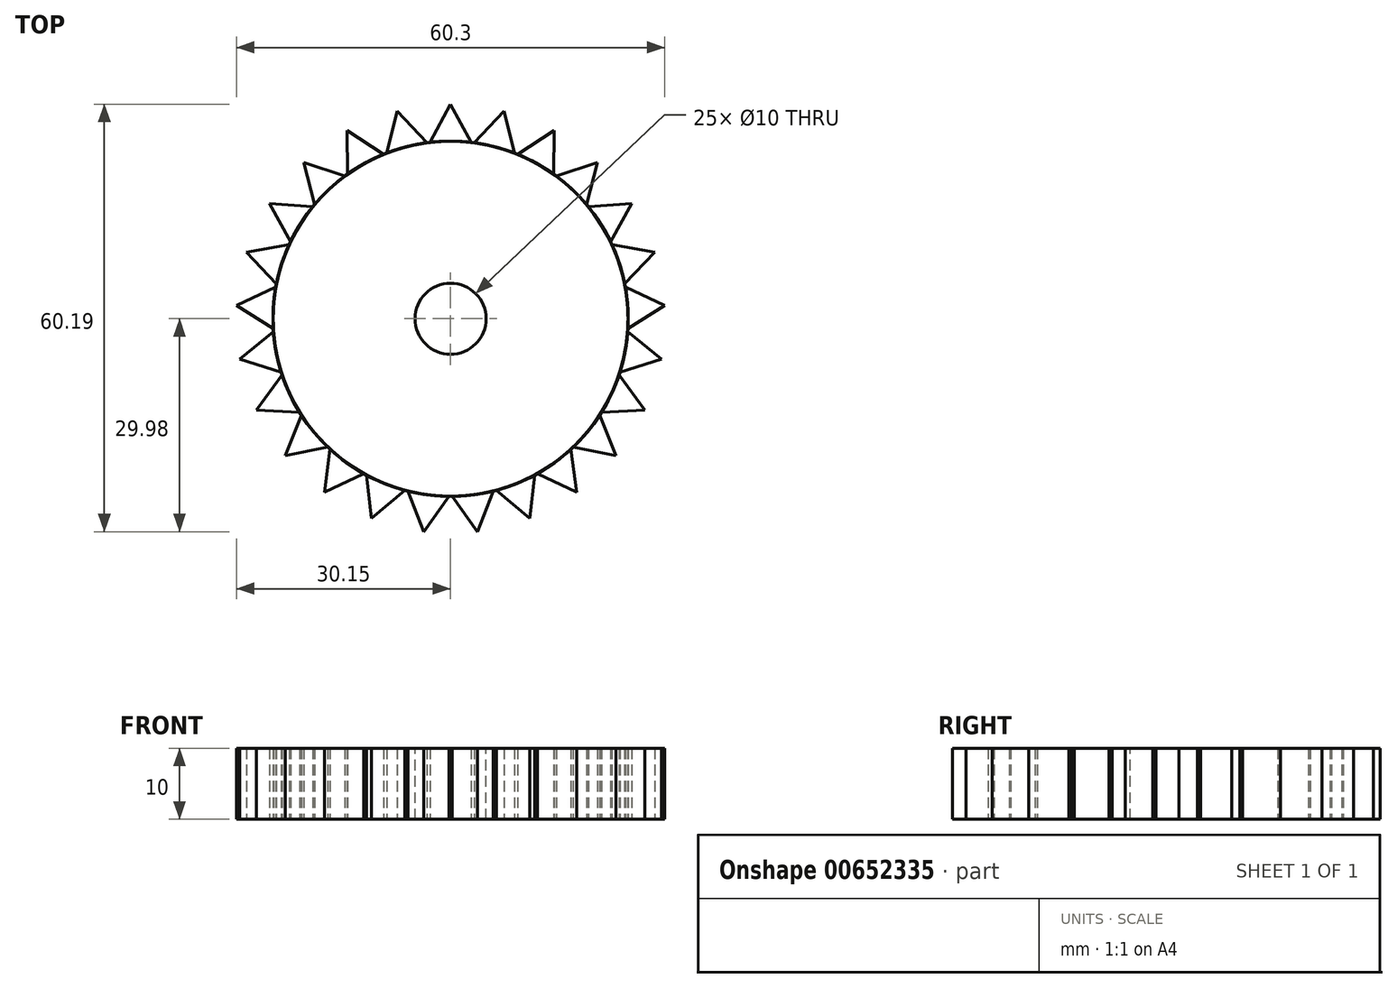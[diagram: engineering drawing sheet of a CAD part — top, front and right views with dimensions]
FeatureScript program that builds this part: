
annotation { "Feature Type Name" : "Feature", "Feature Type Description" : "" }
export const myFeature = defineFeature(function(context is Context, id is Id, definition is map)
    precondition{}
    {
        {
            var Q0;
            Q0=qCreatedBy(makeId("Top.planeOp"),FACE);
            var sketch = newSketch(context, id + "F0", { "sketchPlane" : qUnion([Q0])});
            skCircle(sketch, "E0", {"center": v(0, 0) * mm, "radius": 25 * mm});
            skSolve(sketch);
        }
        {
            var Q0;
            Q0=makeQuery(id+"F0.imprint","IMPRINT",FACE,{"disambiguationData":[TD([[makeQuery(id+"F0.imprint","IMPRINT",EDGE,{"derivedFrom":sQuery(id+"F0.wireOp",EDGE,"E0")}),1.0]])]});
            extrude(context, id + "F1", {"entities" : qUnion([Q0]), "depth" : 10 * mm, "offsetDistance" : 25 * mm});
        }
        {
            var Q0;
            Q0=makeQuery(id+"F1.opExtrude","CAP_FACE",FACE,{"disambiguationData":[OSD([sQuery(id+"F0.wireOp",EDGE,"E0")])],"isStart":false});
            var sketch = newSketch(context, id + "F2", { "sketchPlane" : qUnion([Q0])});
            skCircle(sketch, "E1", {"center": v(0, 0) * mm, "radius": 5 * mm});
            skSolve(sketch);
        }
        {
            var Q0;
            Q0=makeQuery(id+"F2.imprint","IMPRINT",FACE,{"disambiguationData":[TD([[makeQuery(id+"F2.imprint","IMPRINT",EDGE,{"derivedFrom":sQuery(id+"F2.wireOp",EDGE,"E1")}),1.0]])]});
            extrude(context, id + "F3", {"entities" : qUnion([Q0]), "operationType" : NewBodyOperationType.REMOVE, "endBound" : BoundingType.THROUGH_ALL, "oppositeDirection" : true, "depth" : 25 * mm, "offsetDistance" : 25 * mm});
        }
        {
            var Q0;
            Q0=qCreatedBy(makeId("Top.planeOp"),FACE);
            var sketch = newSketch(context, id + "F4", { "sketchPlane" : qUnion([Q0])});
            skLineSegment(sketch, "E2", {"start": v(0, 30.21) * mm, "end": v(-2.91, 24.83) * mm});
            skLineSegment(sketch, "E3", {"start": v(-2.91, 24.83) * mm, "end": v(2.91, 24.83) * mm});
            skLineSegment(sketch, "E4", {"start": v(2.91, 24.83) * mm, "end": v(0, 30.21) * mm});
            skSolve(sketch);
        }
        {
            var Q0;
            Q0=makeQuery(id+"F4.imprint","IMPRINT",FACE,{"disambiguationData":[TD([[makeQuery(id+"F4.imprint","IMPRINT",EDGE,{"derivedFrom":sQuery(id+"F4.wireOp",EDGE,"E2")}),1.0]])]});
            var Q1;
            Q1=qSketchRegion(id+"F6",true);
            extrude(context, id + "F5", {"entities" : qUnion([Q0, Q1]), "operationType" : NewBodyOperationType.ADD, "depth" : 10 * mm, "offsetDistance" : 25 * mm});
        }
        {
            var Q0;
            Q0=makeQuery(id+"F5.boolean.opBoolean","MERGE",FACE,{"derivedFrom":[makeQuery(id+"F1.opExtrude","CAP_FACE",FACE,{"disambiguationData":[OSD([sQuery(id+"F0.wireOp",EDGE,"E0")])],"isStart":false}),makeQuery(id+"F5.opExtrude","CAP_FACE",FACE,{"disambiguationData":[OSD([sQuery(id+"F4.wireOp",EDGE,"E2"),sQuery(id+"F4.wireOp",EDGE,"E3"),sQuery(id+"F4.wireOp",EDGE,"E4")])],"isStart":false})]});
            var sketch = newSketch(context, id + "F6", { "sketchPlane" : qUnion([Q0])});
            skLineSegment(sketch, "E5", {"start": v(-2.91, 24.83) * mm, "end": v(2.91, 24.83) * mm});
            skSolve(sketch);
        }
        {
            var Q0;
            Q0=qCreatedBy(makeId("Right.planeOp"),FACE);
            var sketch = newSketch(context, id + "F7", { "sketchPlane" : qUnion([Q0])});
            skLineSegment(sketch, "E6", {"start": v(0, 26.78) * mm, "end": v(0, -27.9) * mm, "construction": true});
            skSolve(sketch);
        }
        {
            var Q0;
            Q0=makeQuery(id+"F1.opExtrude","SWEPT_BODY",BODY,{"disambiguationData":[OSD([sQuery(id+"F0.wireOp",EDGE,"E0")])]});
            var Q1;
            Q1=sQuery(id+"F7.wireOp",EDGE,"E6");
            circularPattern(context, id + "F8", {"entities" : qUnion([Q0]), "axis" : qUnion([Q1]), "angle" : 360 * degree, "instanceCount" : 25, "equalSpace" : true});
        }
    });
